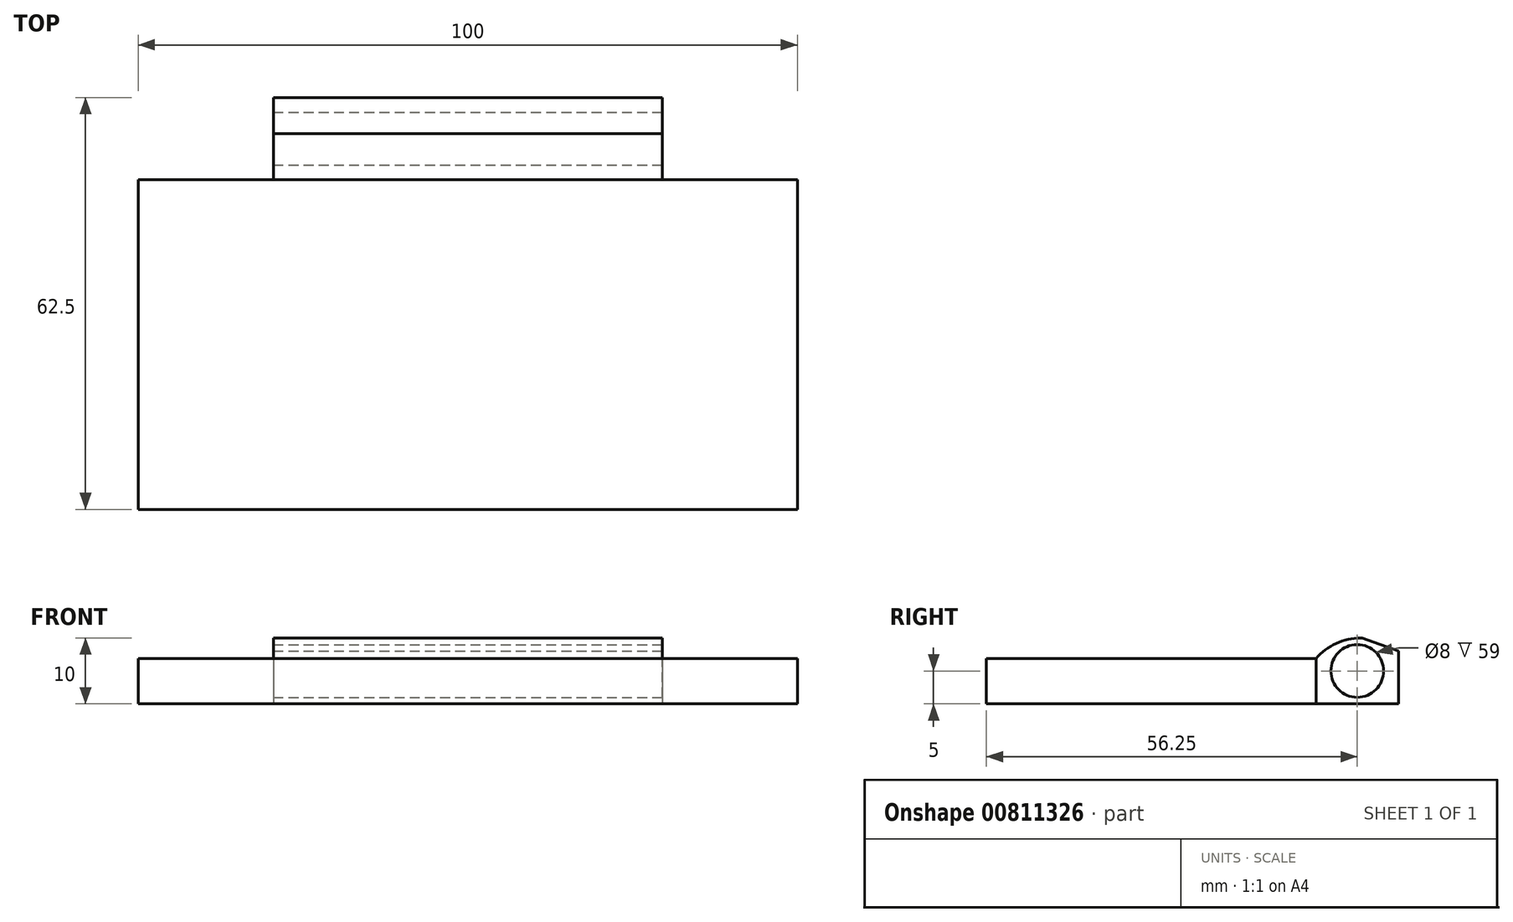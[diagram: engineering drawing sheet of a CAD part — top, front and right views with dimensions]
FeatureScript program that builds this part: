
annotation { "Feature Type Name" : "Feature", "Feature Type Description" : "" }
export const myFeature = defineFeature(function(context is Context, id is Id, definition is map)
    precondition{}
    {
        {
            var Q0;
            Q0=qCreatedBy(makeId("Top.planeOp"),FACE);
            var sketch = newSketch(context, id + "F0", { "sketchPlane" : qUnion([Q0])});
            skLineSegment(sketch, "E0.bottom", {"start": v(50, -25) * mm, "end": v(-50, -25) * mm});
            skLineSegment(sketch, "E0.top", {"start": v(50, 25) * mm, "end": v(-50, 25) * mm});
            skLineSegment(sketch, "E0.left", {"start": v(50, -25) * mm, "end": v(50, 25) * mm});
            skLineSegment(sketch, "E0.right", {"start": v(-50, -25) * mm, "end": v(-50, 25) * mm});
            skPoint(sketch, "E0.middle", {"position": v(0, 0) * mm});
            skLineSegment(sketch, "E1.bottom", {"start": v(-50, 25) * mm, "end": v(-29.5, 25) * mm});
            skLineSegment(sketch, "E1.top", {"start": v(-50, 37.5) * mm, "end": v(-29.5, 37.5) * mm});
            skLineSegment(sketch, "E1.left", {"start": v(-50, 25) * mm, "end": v(-50, 37.5) * mm});
            skLineSegment(sketch, "E1.right", {"start": v(-29.5, 25) * mm, "end": v(-29.5, 37.5) * mm});
            skLineSegment(sketch, "E2.bottom", {"start": v(-29.5, 37.5) * mm, "end": v(29.5, 37.5) * mm});
            skLineSegment(sketch, "E2.top", {"start": v(-29.5, 25) * mm, "end": v(29.5, 25) * mm});
            skLineSegment(sketch, "E2.left", {"start": v(-29.5, 37.5) * mm, "end": v(-29.5, 25) * mm});
            skLineSegment(sketch, "E2.right", {"start": v(29.5, 37.5) * mm, "end": v(29.5, 25) * mm});
            skLineSegment(sketch, "E3.bottom", {"start": v(50, 25) * mm, "end": v(29.5, 25) * mm});
            skLineSegment(sketch, "E3.top", {"start": v(50, 37.5) * mm, "end": v(29.5, 37.5) * mm});
            skLineSegment(sketch, "E3.left", {"start": v(50, 25) * mm, "end": v(50, 37.5) * mm});
            skLineSegment(sketch, "E3.right", {"start": v(29.5, 25) * mm, "end": v(29.5, 37.5) * mm});
            skSolve(sketch);
        }
        {
            var Q0;
            {var subQ2=sQuery(id+"F0.wireOp",EDGE,"E1.right");Q0=makeQuery(id+"F0.imprint","IMPRINT",FACE,{"disambiguationData":[TD([[makeQuery(id+"F0.imprint","IMPRINT",EDGE,{"derivedFrom":subQ2}),-1.0]])]});}
            extrude(context, id + "F1", {"entities" : qUnion([Q0]), "depth" : 10 * mm, "offsetDistance" : 25 * mm});
        }
        {
            var Q0;
            Q0=makeQuery(id+"F0.imprint","IMPRINT",FACE,{"disambiguationData":[TD([[makeQuery(id+"F0.imprint","IMPRINT",EDGE,{"derivedFrom":sQuery(id+"F0.wireOp",EDGE,"E0.bottom")}),-1.0]])]});
            extrude(context, id + "F2", {"entities" : qUnion([Q0]), "operationType" : NewBodyOperationType.ADD, "depth" : 6.9 * mm, "offsetDistance" : 25 * mm});
        }
        {
            var Q0;
            Q0=makeQuery(id+"F1.opExtrude","SWEPT_FACE",FACE,{"disambiguationData":[OSD([sQuery(id+"F0.wireOp",EDGE,"E2.right")])]});
            var sketch = newSketch(context, id + "F3", { "sketchPlane" : qUnion([Q0])});
            skCircle(sketch, "E4", {"center": v(31.25, 5) * mm, "radius": 4 * mm});
            skPoint(sketch, "E4.centerSnap0", {"position": v(37.5, 5) * mm});
            skPoint(sketch, "E4.centerSnap1", {"position": v(31.25, 10) * mm});
            skSolve(sketch);
        }
        {
            var Q0;
            Q0=makeQuery(id+"F3.imprint","IMPRINT",FACE,{"disambiguationData":[TD([[makeQuery(id+"F3.imprint","IMPRINT",EDGE,{"derivedFrom":sQuery(id+"F3.wireOp",EDGE,"E4")}),1.0]])]});
            extrude(context, id + "F4", {"entities" : qUnion([Q0]), "operationType" : NewBodyOperationType.REMOVE, "endBound" : BoundingType.UP_TO_NEXT, "oppositeDirection" : true, "depth" : 25 * mm, "offsetDistance" : 25 * mm});
        }
        {
            var Q0;
            Q0=makeQuery(id+"F1.opExtrude","CAP_EDGE",EDGE,{"disambiguationData":[OSD([sQuery(id+"F0.wireOp",EDGE,"E0.top")])],"isStart":false});
            fillet(context, id + "F5", {"entities" : qUnion([Q0]), "radius" : 9 * mm, "tangentPropagation" : true, "allowEdgeOverflow" : false});
        }
        {
            var Q0;
            Q0=makeQuery(id+"F1.opExtrude","CAP_EDGE",EDGE,{"disambiguationData":[OSD([sQuery(id+"F0.wireOp",EDGE,"E2.bottom")])],"isStart":false});
            chamfer(context, id + "F6", {"entities" : qUnion([Q0]), "chamferType" : ChamferType.OFFSET_ANGLE, "width" : 2 * mm, "oppositeDirection" : false, "angle" : 70 * degree, "tangentPropagation" : true});
        }
    });
